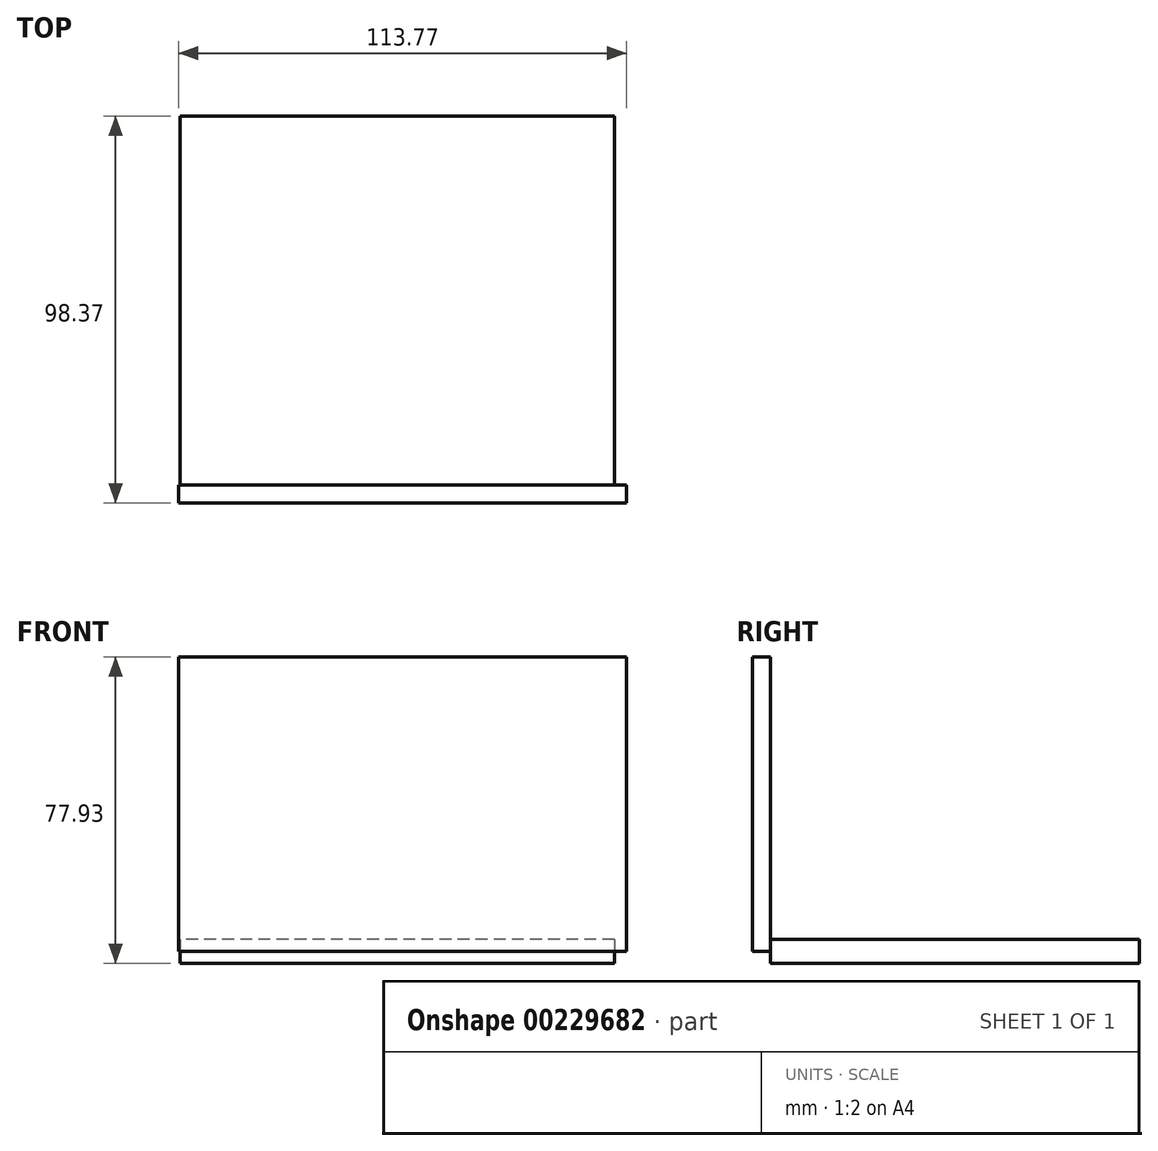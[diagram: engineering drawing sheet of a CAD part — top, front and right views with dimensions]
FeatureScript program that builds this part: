
annotation { "Feature Type Name" : "Feature", "Feature Type Description" : "" }
export const myFeature = defineFeature(function(context is Context, id is Id, definition is map)
    precondition{}
    {
        {
            var Q0;
            Q0=qCreatedBy(makeId("Top.planeOp"),FACE);
            var sketch = newSketch(context, id + "F0", { "sketchPlane" : qUnion([Q0])});
            skLineSegment(sketch, "E0.bottom", {"start": v(55.18, 46.9) * mm, "end": v(-55.18, 46.9) * mm});
            skLineSegment(sketch, "E0.top", {"start": v(55.18, -46.9) * mm, "end": v(-55.18, -46.9) * mm});
            skLineSegment(sketch, "E0.left", {"start": v(55.18, 46.9) * mm, "end": v(55.18, -46.9) * mm});
            skLineSegment(sketch, "E0.right", {"start": v(-55.18, 46.9) * mm, "end": v(-55.18, -46.9) * mm});
            skPoint(sketch, "E0.middle", {"position": v(0, 0) * mm});
            skSolve(sketch);
        }
        {
            var Q0;
            Q0=sQuery(id+"F0.wireOp",EDGE,"E0.top");
            cPlane(context, id + "F1", {"entities" : qUnion([Q0]), "cplaneType" : CPlaneType.LINE_ANGLE, "offset" : 25.4 * mm, "angle" : 0 * degree, "width" : 152.4 * mm, "height" : 152.4 * mm});
        }
        {
            var Q0;
            Q0=qCreatedBy(id+"F1.planeOp",FACE);
            var sketch = newSketch(context, id + "F2", { "sketchPlane" : qUnion([Q0])});
            skLineSegment(sketch, "E1", {"start": v(-55.5, 0) * mm, "end": v(-55.5, 74.88) * mm});
            skLineSegment(sketch, "E2", {"start": v(-55.5, 74.88) * mm, "end": v(58.26, 74.88) * mm});
            skLineSegment(sketch, "E3", {"start": v(58.26, 74.88) * mm, "end": v(58.26, 0) * mm});
            skLineSegment(sketch, "E4", {"start": v(58.26, 0) * mm, "end": v(-55.5, 0) * mm});
            skSolve(sketch);
        }
        {
            var Q0;
            Q0=makeQuery(id+"F0.imprint","IMPRINT",FACE,{"disambiguationData":[TD([[makeQuery(id+"F0.imprint","IMPRINT",EDGE,{"derivedFrom":sQuery(id+"F0.wireOp",EDGE,"E0.bottom")}),1.0]])]});
            extrude(context, id + "F3", {"entities" : qUnion([Q0]), "endBound" : BoundingType.SYMMETRIC, "depth" : 6.1 * mm});
        }
        {
            var Q0;
            Q0=makeQuery(id+"F2.imprint","IMPRINT",FACE,{"disambiguationData":[TD([[makeQuery(id+"F2.imprint","IMPRINT",EDGE,{"derivedFrom":sQuery(id+"F2.wireOp",EDGE,"E1")}),-1.0]])]});
            extrude(context, id + "F4", {"entities" : qUnion([Q0]), "operationType" : NewBodyOperationType.ADD, "depth" : 4.57 * mm});
        }
    });
